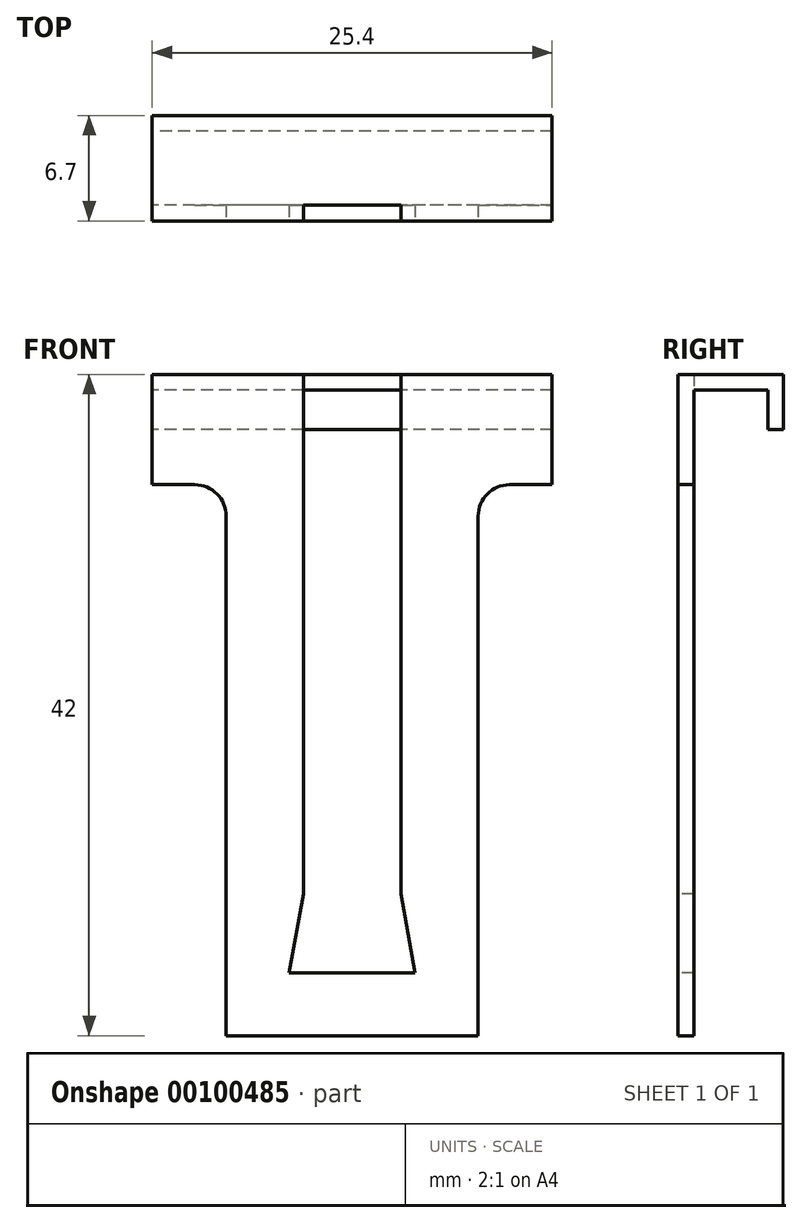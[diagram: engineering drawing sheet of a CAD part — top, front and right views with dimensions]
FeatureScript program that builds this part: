
annotation { "Feature Type Name" : "Feature", "Feature Type Description" : "" }
export const myFeature = defineFeature(function(context is Context, id is Id, definition is map)
    precondition{}
    {
        {
            var Q0;
            Q0=qCreatedBy(makeId("Right.planeOp"),FACE);
            var sketch = newSketch(context, id + "F0", { "sketchPlane" : qUnion([Q0])});
            skLineSegment(sketch, "E0", {"start": v(0, 0) * mm, "end": v(6.7, 0) * mm});
            skLineSegment(sketch, "E1", {"start": v(6.7, 0) * mm, "end": v(6.7, -3.5) * mm});
            skLineSegment(sketch, "E2", {"start": v(6.7, -3.5) * mm, "end": v(5.7, -3.5) * mm});
            skLineSegment(sketch, "E3", {"start": v(5.7, -3.5) * mm, "end": v(5.7, -1) * mm});
            skLineSegment(sketch, "E4", {"start": v(5.7, -1) * mm, "end": v(1, -1) * mm});
            skLineSegment(sketch, "E5", {"start": v(1, -1) * mm, "end": v(1, -42) * mm});
            skLineSegment(sketch, "E6", {"start": v(1, -42) * mm, "end": v(0, -42) * mm});
            skLineSegment(sketch, "E7", {"start": v(0, -42) * mm, "end": v(0, 0) * mm});
            skSolve(sketch);
        }
        {
            var Q0;
            Q0 = qSketchRegion(id + "F0", true);
            extrude(context, id + "F1", {"entities" : qUnion([Q0]), "endBound" : BoundingType.SYMMETRIC, "depth" : 25.4 * mm});
        }
        {
            var Q0;
            Q0=makeQuery(id+"F1.opExtrude","SWEPT_FACE",FACE,{"disambiguationData":[OSD([sQuery(id+"F0.wireOp",EDGE,"E7")])]});
            var sketch = newSketch(context, id + "F2", { "sketchPlane" : qUnion([Q0])});
            skLineSegment(sketch, "E8", {"start": v(-3.1, 0) * mm, "end": v(-3.1, -33) * mm});
            skLineSegment(sketch, "E9", {"start": v(3.1, 0) * mm, "end": v(3.1, -33) * mm});
            skLineSegment(sketch, "E10", {"start": v(-4, -38) * mm, "end": v(4, -38) * mm});
            skLineSegment(sketch, "E11", {"start": v(-4, -38) * mm, "end": v(-3.1, -33) * mm});
            skLineSegment(sketch, "E12", {"start": v(4, -38) * mm, "end": v(3.1, -33) * mm});
            skLineSegment(sketch, "E13", {"start": v(3.1, 0) * mm, "end": v(-3.1, 0) * mm});
            skLineSegment(sketch, "E14", {"start": v(-8, -42) * mm, "end": v(-8, -7) * mm});
            skLineSegment(sketch, "E15", {"start": v(8, -42) * mm, "end": v(8, -7) * mm});
            skLineSegment(sketch, "E16", {"start": v(-4, -38) * mm, "end": v(-4, -42) * mm, "construction": true});
            skLineSegment(sketch, "E17", {"start": v(-4, -38) * mm, "end": v(-8, -38) * mm, "construction": true});
            skLineSegment(sketch, "E18", {"start": v(8, -7) * mm, "end": v(12.7, -7) * mm});
            skLineSegment(sketch, "E19", {"start": v(-8, -7) * mm, "end": v(-12.7, -7) * mm});
            skLineSegment(sketch, "E20", {"start": v(-12.7, -7) * mm, "end": v(-12.7, -42) * mm});
            skLineSegment(sketch, "E21", {"start": v(-12.7, -42) * mm, "end": v(-8, -42) * mm});
            skLineSegment(sketch, "E22", {"start": v(8, -42) * mm, "end": v(12.7, -42) * mm});
            skLineSegment(sketch, "E23", {"start": v(12.7, -42) * mm, "end": v(12.7, -7) * mm});
            skSolve(sketch);
        }
        {
            var Q0;
            Q0 = qSketchRegion(id + "F2", true);
            var Q1;
            Q1=makeQuery(id+"F1.opExtrude","SWEPT_FACE",FACE,{"disambiguationData":[OSD([sQuery(id+"F0.wireOp",EDGE,"E5")])]});
            extrude(context, id + "F3", {"entities" : qUnion([Q0]), "operationType" : NewBodyOperationType.REMOVE, "endBound" : BoundingType.UP_TO_SURFACE, "oppositeDirection" : true, "endBoundEntityFace" : qUnion([Q1]), "depth" : 25 * mm});
        }
        {
            var Q0;
            Q0=makeQuery(id+"F3.boolean.opBoolean","COPY",EDGE,{"derivedFrom":makeQuery(id+"F3.opExtrude","SWEPT_EDGE",EDGE,{"disambiguationData":[OSD([sQuery(id+"F0.wireOp",EDGE,"E6"),sQuery(id+"F0.wireOp",EDGE,"E7"),sQuery(id+"F2.wireOp",EDGE,"E15"),sQuery(id+"F2.wireOp",EDGE,"E22")])]})});
            var Q1;
            Q1=makeQuery(id+"F3.boolean.opBoolean","COPY",EDGE,{"derivedFrom":makeQuery(id+"F3.opExtrude","SWEPT_EDGE",EDGE,{"disambiguationData":[OSD([sQuery(id+"F0.wireOp",EDGE,"E6"),sQuery(id+"F0.wireOp",EDGE,"E7"),sQuery(id+"F2.wireOp",EDGE,"E14"),sQuery(id+"F2.wireOp",EDGE,"E21")])]})});
            var Q2;
            Q2=makeQuery(id+"F3.boolean.opBoolean","COPY",EDGE,{"derivedFrom":makeQuery(id+"F3.opExtrude","SWEPT_EDGE",EDGE,{"disambiguationData":[OSD([sQuery(id+"F2.wireOp",EDGE,"E14"),sQuery(id+"F2.wireOp",EDGE,"E19")])]})});
            var Q3;
            Q3=makeQuery(id+"F3.boolean.opBoolean","COPY",EDGE,{"derivedFrom":makeQuery(id+"F3.opExtrude","SWEPT_EDGE",EDGE,{"disambiguationData":[OSD([sQuery(id+"F0.wireOp",EDGE,"E7"),sQuery(id+"F2.wireOp",EDGE,"E19"),sQuery(id+"F2.wireOp",EDGE,"E20")])]})});
            var Q4;
            Q4=makeQuery(id+"F3.boolean.opBoolean","COPY",EDGE,{"derivedFrom":makeQuery(id+"F3.opExtrude","SWEPT_EDGE",EDGE,{"disambiguationData":[OSD([sQuery(id+"F2.wireOp",EDGE,"E15"),sQuery(id+"F2.wireOp",EDGE,"E18")])]})});
            var Q5;
            Q5=makeQuery(id+"F3.boolean.opBoolean","COPY",EDGE,{"derivedFrom":makeQuery(id+"F3.opExtrude","SWEPT_EDGE",EDGE,{"disambiguationData":[OSD([sQuery(id+"F0.wireOp",EDGE,"E7"),sQuery(id+"F2.wireOp",EDGE,"E18"),sQuery(id+"F2.wireOp",EDGE,"E23")])]})});
            fillet(context, id + "F4", {"entities" : qUnion([Q0, Q1, Q2, Q3, Q4, Q5]), "radius" : 2 * mm, "tangentPropagation" : true, "allowEdgeOverflow" : false});
        }
    });
